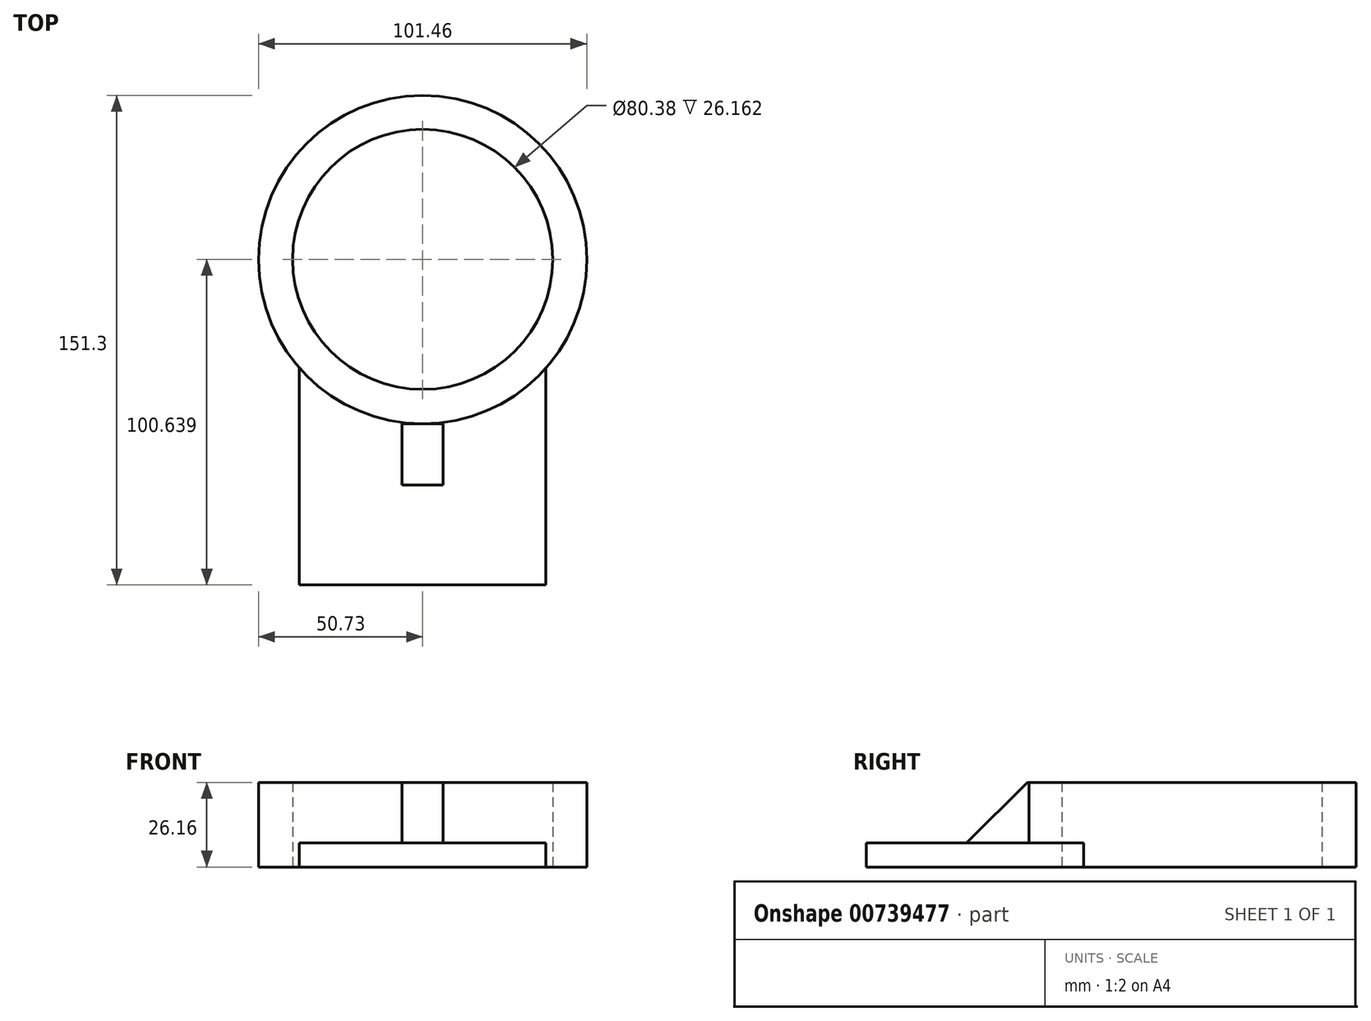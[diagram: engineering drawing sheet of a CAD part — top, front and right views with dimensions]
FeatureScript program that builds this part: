
annotation { "Feature Type Name" : "Feature", "Feature Type Description" : "" }
export const myFeature = defineFeature(function(context is Context, id is Id, definition is map)
    precondition{}
    {
        {
            var Q0;
            Q0=qCreatedBy(makeId("Right.planeOp"),FACE);
            var sketch = newSketch(context, id + "F0", { "sketchPlane" : qUnion([Q0])});
            skLineSegment(sketch, "E0.bottom", {"start": v(0, 0) * mm, "end": v(-49.77, 0) * mm});
            skLineSegment(sketch, "E0.top", {"start": v(0, 7.49) * mm, "end": v(-49.77, 7.49) * mm});
            skLineSegment(sketch, "E0.left", {"start": v(0, 0) * mm, "end": v(0, 7.49) * mm});
            skLineSegment(sketch, "E0.right", {"start": v(-49.77, 0) * mm, "end": v(-49.77, 7.49) * mm});
            skLineSegment(sketch, "E1", {"start": v(0, 7.49) * mm, "end": v(0, 26.07) * mm});
            skLineSegment(sketch, "E2", {"start": v(0, 26.07) * mm, "end": v(-18.86, 7.49) * mm});
            skLineSegment(sketch, "E3", {"start": v(-18.86, 7.49) * mm, "end": v(0, 7.49) * mm});
            skSolve(sketch);
        }
        {
            var Q0;
            Q0=makeQuery(id+"F0.imprint","IMPRINT",FACE,{"disambiguationData":[TD([[makeQuery(id+"F0.imprint","IMPRINT",EDGE,{"derivedFrom":sQuery(id+"F0.wireOp",EDGE,"E0.bottom")}),-1.0]])]});
            extrude(context, id + "F1", {"entities" : qUnion([Q0]), "depth" : 6.35 * mm, "offsetDistance" : 25.4 * mm});
        }
        {
            var Q0;
            Q0=makeQuery(id+"F0.imprint","IMPRINT",FACE,{"disambiguationData":[TD([[makeQuery(id+"F0.imprint","IMPRINT",EDGE,{"derivedFrom":sQuery(id+"F0.wireOp",EDGE,"E0.bottom")}),-1.0]])]});
            extrude(context, id + "F2", {"entities" : qUnion([Q0]), "operationType" : NewBodyOperationType.ADD, "oppositeDirection" : true, "depth" : 6.35 * mm, "offsetDistance" : 25.4 * mm});
        }
        {
            var Q0;
            Q0=makeQuery(id+"F2.opExtrude","CAP_FACE",FACE,{"disambiguationData":[OSD([sQuery(id+"F0.wireOp",EDGE,"E0.bottom"),sQuery(id+"F0.wireOp",EDGE,"E0.top"),sQuery(id+"F0.wireOp",EDGE,"E0.left"),sQuery(id+"F0.wireOp",EDGE,"E0.right"),sQuery(id+"F0.wireOp",EDGE,"E3")])],"isStart":false});
            var Q1;
            Q1=makeQuery(id+"F1.opExtrude","CAP_FACE",FACE,{"disambiguationData":[OSD([sQuery(id+"F0.wireOp",EDGE,"E0.bottom"),sQuery(id+"F0.wireOp",EDGE,"E0.top"),sQuery(id+"F0.wireOp",EDGE,"E0.left"),sQuery(id+"F0.wireOp",EDGE,"E0.right"),sQuery(id+"F0.wireOp",EDGE,"E3")])],"isStart":false});
            extrude(context, id + "F3", {"entities" : qUnion([Q0, Q1]), "operationType" : NewBodyOperationType.ADD, "oppositeDirection" : true, "depth" : 6.35 * mm, "offsetDistance" : 25.4 * mm});
        }
        {
            var Q0;
            Q0=makeQuery(id+"F2.opExtrude","CAP_FACE",FACE,{"disambiguationData":[OSD([sQuery(id+"F0.wireOp",EDGE,"E0.bottom"),sQuery(id+"F0.wireOp",EDGE,"E0.top"),sQuery(id+"F0.wireOp",EDGE,"E0.left"),sQuery(id+"F0.wireOp",EDGE,"E0.right"),sQuery(id+"F0.wireOp",EDGE,"E3")])],"isStart":false});
            extrude(context, id + "F4", {"entities" : qUnion([Q0]), "operationType" : NewBodyOperationType.ADD, "depth" : 6.35 * mm, "offsetDistance" : 25.4 * mm});
        }
        {
            var Q0;
            Q0=makeQuery(id+"F0.imprint","IMPRINT",FACE,{"disambiguationData":[TD([[makeQuery(id+"F0.imprint","IMPRINT",EDGE,{"derivedFrom":sQuery(id+"F0.wireOp",EDGE,"E1")}),1.0]])]});
            extrude(context, id + "F5", {"entities" : qUnion([Q0]), "operationType" : NewBodyOperationType.ADD, "depth" : 6.35 * mm, "offsetDistance" : 25.4 * mm});
        }
        {
            var Q0;
            Q0=makeQuery(id+"F0.imprint","IMPRINT",FACE,{"disambiguationData":[TD([[makeQuery(id+"F0.imprint","IMPRINT",EDGE,{"derivedFrom":sQuery(id+"F0.wireOp",EDGE,"E1")}),1.0]])]});
            extrude(context, id + "F6", {"entities" : qUnion([Q0]), "operationType" : NewBodyOperationType.ADD, "oppositeDirection" : true, "depth" : 6.35 * mm, "offsetDistance" : 25.4 * mm});
        }
        {
            var Q0;
            {var subQ0=sQuery(id+"F0.wireOp",EDGE,"E3");var subQ1=sQuery(id+"F0.wireOp",EDGE,"E0.right");var subQ2=sQuery(id+"F0.wireOp",EDGE,"E0.left");var subQ3=sQuery(id+"F0.wireOp",EDGE,"E0.top");var subQ4=sQuery(id+"F0.wireOp",EDGE,"E0.bottom");Q0=makeQuery(id+"F3.opExtrude","CAP_FACE",FACE,{"disambiguationData":[OSD([subQ4,subQ3,subQ2,subQ1,subQ0]),TDD([makeQuery(id+"F1.opExtrude","CAP_FACE",FACE,{"disambiguationData":[OSD([subQ4,subQ3,subQ2,subQ1,subQ0])],"isStart":false})])],"isStart":false});}
            extrude(context, id + "F7", {"entities" : qUnion([Q0]), "operationType" : NewBodyOperationType.ADD, "depth" : 25.4 * mm, "offsetDistance" : 25.4 * mm});
        }
        {
            var Q0;
            Q0=makeQuery(id+"F4.opExtrude","CAP_FACE",FACE,{"disambiguationData":[OSD([sQuery(id+"F0.wireOp",EDGE,"E0.bottom"),sQuery(id+"F0.wireOp",EDGE,"E0.top"),sQuery(id+"F0.wireOp",EDGE,"E0.left"),sQuery(id+"F0.wireOp",EDGE,"E0.right"),sQuery(id+"F0.wireOp",EDGE,"E3")])],"isStart":false});
            extrude(context, id + "F8", {"entities" : qUnion([Q0]), "operationType" : NewBodyOperationType.ADD, "depth" : 25.4 * mm, "offsetDistance" : 25.4 * mm});
        }
        {
            var Q0;
            {var subQ0=sQuery(id+"F0.wireOp",EDGE,"E0.left");var subQ1=sQuery(id+"F0.wireOp",EDGE,"E1");Q0=makeQuery(id+"F8.boolean.opBoolean","MERGE",FACE,{"derivedFrom":[makeQuery(id+"F7.boolean.opBoolean","MERGE",FACE,{"derivedFrom":[makeQuery(id+"F6.boolean.opBoolean","MERGE",FACE,{"derivedFrom":[makeQuery(id+"F5.boolean.opBoolean","MERGE",FACE,{"derivedFrom":[makeQuery(id+"F4.boolean.opBoolean","MERGE",FACE,{"derivedFrom":[makeQuery(id+"F3.boolean.opBoolean","MERGE",FACE,{"derivedFrom":[makeQuery(id+"F2.boolean.opBoolean","MERGE",FACE,{"derivedFrom":[makeQuery(id+"F1.opExtrude","SWEPT_FACE",FACE,{"disambiguationData":[OSD([subQ0])]}),makeQuery(id+"F2.opExtrude","SWEPT_FACE",FACE,{"disambiguationData":[OSD([subQ0])]})]}),makeQuery(id+"F3.opExtrude","SWEPT_FACE",FACE,{"disambiguationData":[OSD([subQ0]),TDD([makeQuery(id+"F1.opExtrude","CAP_EDGE",EDGE,{"disambiguationData":[OSD([subQ0])],"isStart":false})])]})]}),makeQuery(id+"F4.opExtrude","SWEPT_FACE",FACE,{"disambiguationData":[OSD([subQ0])]})]}),makeQuery(id+"F5.opExtrude","SWEPT_FACE",FACE,{"disambiguationData":[OSD([subQ1])]})]}),makeQuery(id+"F6.opExtrude","SWEPT_FACE",FACE,{"disambiguationData":[OSD([subQ1])]})]}),makeQuery(id+"F7.opExtrude","SWEPT_FACE",FACE,{"disambiguationData":[OSD([subQ0])]})]}),makeQuery(id+"F8.opExtrude","SWEPT_FACE",FACE,{"disambiguationData":[OSD([subQ0])]})]});}
            extrude(context, id + "F9", {"entities" : qUnion([Q0]), "operationType" : NewBodyOperationType.ADD, "depth" : 50.8 * mm, "offsetDistance" : 25.4 * mm});
        }
        {
            var Q0;
            {var subQ0=sQuery(id+"F0.wireOp",EDGE,"E0.bottom");Q0=makeQuery(id+"F9.boolean.opBoolean","MERGE",FACE,{"derivedFrom":[makeQuery(id+"F8.boolean.opBoolean","MERGE",FACE,{"derivedFrom":[makeQuery(id+"F7.boolean.opBoolean","MERGE",FACE,{"derivedFrom":[makeQuery(id+"F4.boolean.opBoolean","MERGE",FACE,{"derivedFrom":[makeQuery(id+"F3.boolean.opBoolean","MERGE",FACE,{"derivedFrom":[makeQuery(id+"F2.boolean.opBoolean","MERGE",FACE,{"derivedFrom":[makeQuery(id+"F1.opExtrude","SWEPT_FACE",FACE,{"disambiguationData":[OSD([subQ0])]}),makeQuery(id+"F2.opExtrude","SWEPT_FACE",FACE,{"disambiguationData":[OSD([subQ0])]})]}),makeQuery(id+"F3.opExtrude","SWEPT_FACE",FACE,{"disambiguationData":[OSD([subQ0]),TDD([makeQuery(id+"F1.opExtrude","CAP_EDGE",EDGE,{"disambiguationData":[OSD([subQ0])],"isStart":false})])]})]}),makeQuery(id+"F4.opExtrude","SWEPT_FACE",FACE,{"disambiguationData":[OSD([subQ0])]})]}),makeQuery(id+"F7.opExtrude","SWEPT_FACE",FACE,{"disambiguationData":[OSD([subQ0])]})]}),makeQuery(id+"F8.opExtrude","SWEPT_FACE",FACE,{"disambiguationData":[OSD([subQ0])]})]}),makeQuery(id+"F9.opExtrude","SWEPT_FACE",FACE,{"disambiguationData":[OSD([subQ0,sQuery(id+"F0.wireOp",EDGE,"E0.left")])]})]});}
            var sketch = newSketch(context, id + "F10", { "sketchPlane" : qUnion([Q0])});
            skPoint(sketch, "E4.center.orphan", {"position": v(0, 25.5) * mm});
            skPoint(sketch, "E5.center.orphan", {"position": v(0, 25.88) * mm});
            skPoint(sketch, "E6.center.orphan", {"position": v(0, -24.74) * mm});
            skCircle(sketch, "E7", {"center": v(0, -50.8) * mm, "radius": 50.73 * mm});
            skSolve(sketch);
        }
        {
            var Q0;
            {var subQ1=sQuery(id+"F0.wireOp",EDGE,"E0.left");var subQ2=sQuery(id+"F0.wireOp",EDGE,"E0.bottom");var subQ7=makeQuery(id+"F9.opExtrude","CAP_EDGE",EDGE,{"disambiguationData":[OSD([subQ2,subQ1])],"isStart":false});Q0=makeQuery(id+"F10.imprint","IMPRINT",FACE,{"disambiguationData":[TD([[makeQuery(id+"F10.imprint","IMPRINT",EDGE,{"derivedFrom":subQ7}),-1.0]])]});}
            extrude(context, id + "F11", {"entities" : qUnion([Q0]), "operationType" : NewBodyOperationType.ADD, "oppositeDirection" : true, "depth" : 26.16 * mm, "offsetDistance" : 25.4 * mm});
        }
        {
            var Q0;
            {var subQ1=sQuery(id+"F0.wireOp",EDGE,"E0.left");var subQ2=sQuery(id+"F0.wireOp",EDGE,"E0.bottom");var subQ7=makeQuery(id+"F9.opExtrude","CAP_EDGE",EDGE,{"disambiguationData":[OSD([subQ2,subQ1])],"isStart":false});Q0=makeQuery(id+"F10.imprint","IMPRINT",FACE,{"disambiguationData":[TD([[makeQuery(id+"F10.imprint","IMPRINT",EDGE,{"derivedFrom":subQ7}),1.0]])]});}
            extrude(context, id + "F12", {"entities" : qUnion([Q0]), "operationType" : NewBodyOperationType.ADD, "oppositeDirection" : true, "depth" : 26.16 * mm, "offsetDistance" : 25.4 * mm});
        }
        {
            var Q0;
            {var subQ1=sQuery(id+"F0.wireOp",EDGE,"E0.left");var subQ2=sQuery(id+"F0.wireOp",EDGE,"E0.bottom");var subQ7=makeQuery(id+"F9.opExtrude","CAP_EDGE",EDGE,{"disambiguationData":[OSD([subQ2,subQ1])],"isStart":false});Q0=makeQuery(id+"F10.imprint","IMPRINT",FACE,{"disambiguationData":[TD([[makeQuery(id+"F10.imprint","IMPRINT",EDGE,{"derivedFrom":subQ7}),1.0]])]});}
            var sketch = newSketch(context, id + "F13", { "sketchPlane" : qUnion([Q0])});
            skCircle(sketch, "E8", {"center": v(0, -50.87) * mm, "radius": 40.2 * mm});
            skSolve(sketch);
        }
        {
            var Q0;
            {var subQ1=sQuery(id+"F0.wireOp",EDGE,"E0.left");var subQ2=sQuery(id+"F0.wireOp",EDGE,"E0.bottom");var subQ4=makeQuery(id+"F9.opExtrude","CAP_EDGE",EDGE,{"disambiguationData":[OSD([subQ2,subQ1])],"isStart":false});var subQ11=makeQuery(id+"F10.imprint","IMPRINT",EDGE,{"derivedFrom":subQ4});Q0=makeQuery(id+"F13.imprint","IMPRINT",FACE,{"disambiguationData":[TD([[makeQuery(id+"F13.imprint","IMPRINT",EDGE,{"derivedFrom":subQ11}),-1.0]])]});}
            extrude(context, id + "F14", {"entities" : qUnion([Q0]), "operationType" : NewBodyOperationType.REMOVE, "oppositeDirection" : true, "depth" : 254 * mm, "offsetDistance" : 25.4 * mm});
        }
        {
            var Q0;
            Q0 = qSketchRegion(id + "F13", true);
            extrude(context, id + "F15", {"entities" : qUnion([Q0]), "operationType" : NewBodyOperationType.REMOVE, "oppositeDirection" : true, "depth" : 254 * mm, "offsetDistance" : 25.4 * mm});
        }
    });
